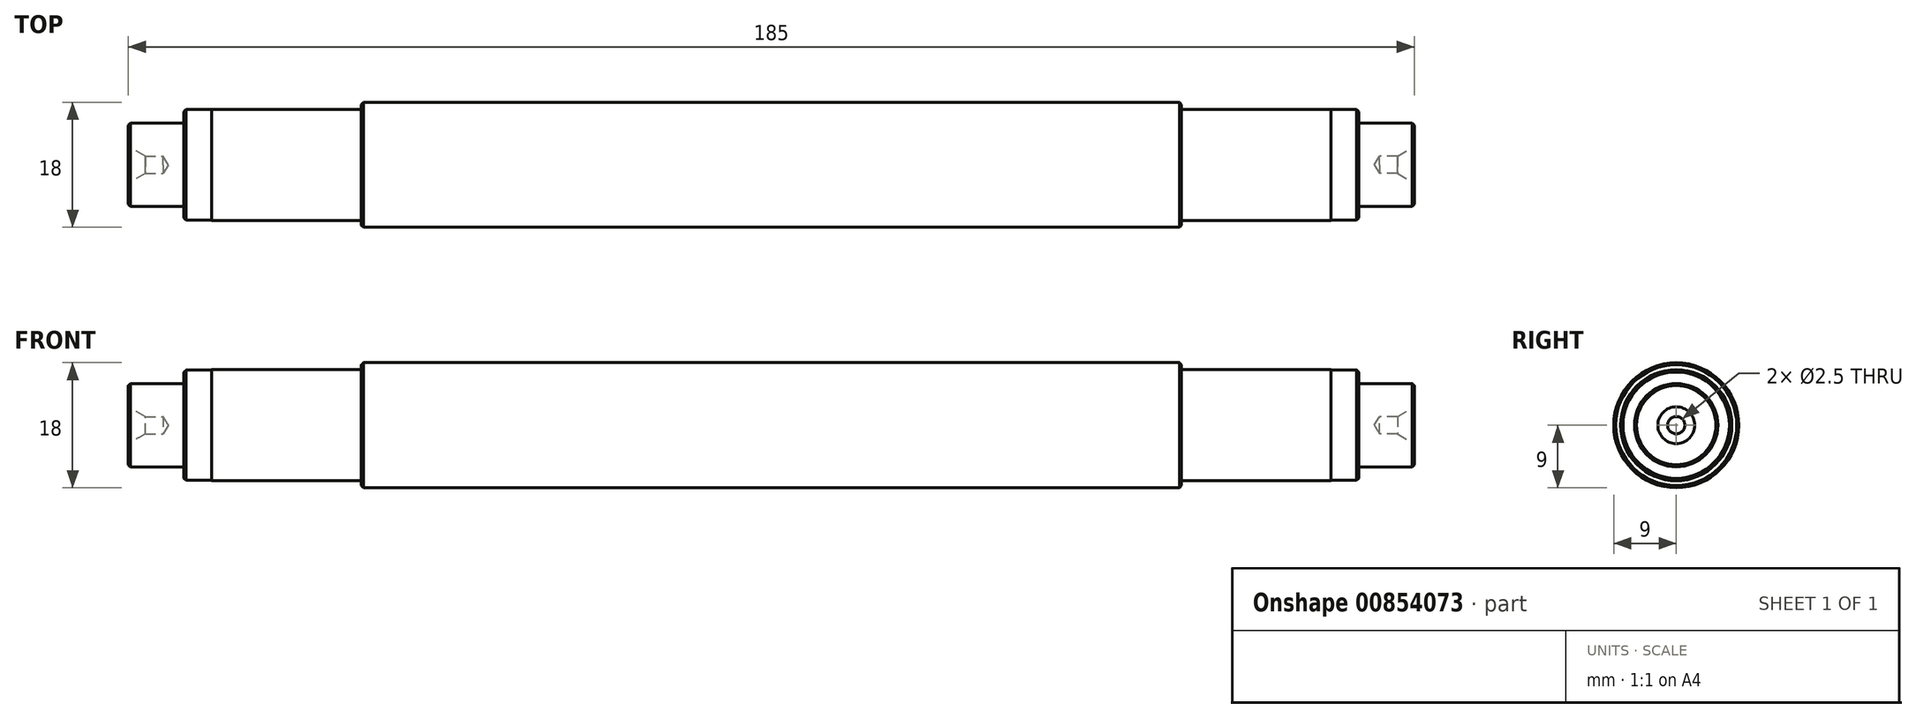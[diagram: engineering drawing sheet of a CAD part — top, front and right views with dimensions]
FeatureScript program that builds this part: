
annotation { "Feature Type Name" : "Feature", "Feature Type Description" : "" }
export const myFeature = defineFeature(function(context is Context, id is Id, definition is map)
    precondition{}
    {
        {
            var Q0;
            Q0=qCreatedBy(makeId("Top.planeOp"),FACE);
            var sketch = newSketch(context, id + "F0", { "sketchPlane" : qUnion([Q0])});
            skLineSegment(sketch, "E0.bottom", {"start": v(0, 0) * mm, "end": v(118, 0) * mm});
            skLineSegment(sketch, "E0.top", {"start": v(0, 9) * mm, "end": v(118, 9) * mm});
            skLineSegment(sketch, "E0.left", {"start": v(0, 0) * mm, "end": v(0, 9) * mm});
            skLineSegment(sketch, "E0.right", {"start": v(118, 0) * mm, "end": v(118, 9) * mm});
            skLineSegment(sketch, "E1.bottom", {"start": v(0, 0) * mm, "end": v(-21.5, 0) * mm});
            skLineSegment(sketch, "E1.top", {"start": v(0, 8) * mm, "end": v(-21.5, 8) * mm});
            skLineSegment(sketch, "E1.left", {"start": v(0, 0) * mm, "end": v(0, 8) * mm});
            skLineSegment(sketch, "E1.right", {"start": v(-21.5, 0) * mm, "end": v(-21.5, 8) * mm});
            skLineSegment(sketch, "E2.bottom", {"start": v(118, 0) * mm, "end": v(139.5, 0) * mm});
            skLineSegment(sketch, "E2.top", {"start": v(118, 8) * mm, "end": v(139.5, 8) * mm});
            skLineSegment(sketch, "E2.left", {"start": v(118, 0) * mm, "end": v(118, 8) * mm});
            skLineSegment(sketch, "E2.right", {"start": v(139.5, 0) * mm, "end": v(139.5, 8) * mm});
            skLineSegment(sketch, "E3.bottom", {"start": v(-21.5, 0) * mm, "end": v(-25.5, 0) * mm});
            skLineSegment(sketch, "E3.top", {"start": v(-21.5, 7.95) * mm, "end": v(-25.5, 7.95) * mm});
            skLineSegment(sketch, "E3.left", {"start": v(-21.5, 0) * mm, "end": v(-21.5, 7.95) * mm});
            skLineSegment(sketch, "E3.right", {"start": v(-25.5, 0) * mm, "end": v(-25.5, 7.95) * mm});
            skLineSegment(sketch, "E4.bottom", {"start": v(139.5, 0) * mm, "end": v(143.5, 0) * mm});
            skLineSegment(sketch, "E4.top", {"start": v(139.5, 7.95) * mm, "end": v(143.5, 7.95) * mm});
            skLineSegment(sketch, "E4.left", {"start": v(139.5, 0) * mm, "end": v(139.5, 7.95) * mm});
            skLineSegment(sketch, "E4.right", {"start": v(143.5, 0) * mm, "end": v(143.5, 7.95) * mm});
            skLineSegment(sketch, "E5.bottom", {"start": v(-25.5, 0) * mm, "end": v(-33.5, 0) * mm});
            skLineSegment(sketch, "E5.top", {"start": v(-25.5, 6) * mm, "end": v(-33.5, 6) * mm});
            skLineSegment(sketch, "E5.left", {"start": v(-25.5, 0) * mm, "end": v(-25.5, 6) * mm});
            skLineSegment(sketch, "E5.right", {"start": v(-33.5, 0) * mm, "end": v(-33.5, 6) * mm});
            skLineSegment(sketch, "E6.bottom", {"start": v(143.5, 0) * mm, "end": v(151.5, 0) * mm});
            skLineSegment(sketch, "E6.top", {"start": v(143.5, 6) * mm, "end": v(151.5, 6) * mm});
            skLineSegment(sketch, "E6.left", {"start": v(143.5, 0) * mm, "end": v(143.5, 6) * mm});
            skLineSegment(sketch, "E6.right", {"start": v(151.5, 0) * mm, "end": v(151.5, 6) * mm});
            skPoint(sketch, "E7", {"position": v(151.5, 0) * mm});
            skPoint(sketch, "E8", {"position": v(-33.5, 0) * mm});
            skSolve(sketch);
        }
        {
            var Q0;
            Q0=makeQuery(id+"F0.imprint","IMPRINT",FACE,{"disambiguationData":[TD([[makeQuery(id+"F0.imprint","IMPRINT",EDGE,{"derivedFrom":sQuery(id+"F0.wireOp",EDGE,"E6.bottom")}),1.0]])]});
            var Q1;
            Q1=makeQuery(id+"F0.imprint","IMPRINT",FACE,{"disambiguationData":[TD([[makeQuery(id+"F0.imprint","IMPRINT",EDGE,{"derivedFrom":sQuery(id+"F0.wireOp",EDGE,"E4.bottom")}),1.0]])]});
            var Q2;
            Q2=makeQuery(id+"F0.imprint","IMPRINT",FACE,{"disambiguationData":[TD([[makeQuery(id+"F0.imprint","IMPRINT",EDGE,{"derivedFrom":sQuery(id+"F0.wireOp",EDGE,"E2.bottom")}),1.0]])]});
            var Q3;
            Q3=makeQuery(id+"F0.imprint","IMPRINT",FACE,{"disambiguationData":[TD([[makeQuery(id+"F0.imprint","IMPRINT",EDGE,{"derivedFrom":sQuery(id+"F0.wireOp",EDGE,"E0.bottom")}),1.0]])]});
            var Q4;
            Q4=makeQuery(id+"F0.imprint","IMPRINT",FACE,{"disambiguationData":[TD([[makeQuery(id+"F0.imprint","IMPRINT",EDGE,{"derivedFrom":sQuery(id+"F0.wireOp",EDGE,"E1.bottom")}),-1.0]])]});
            var Q5;
            Q5=makeQuery(id+"F0.imprint","IMPRINT",FACE,{"disambiguationData":[TD([[makeQuery(id+"F0.imprint","IMPRINT",EDGE,{"derivedFrom":sQuery(id+"F0.wireOp",EDGE,"E3.bottom")}),-1.0]])]});
            var Q6;
            Q6=makeQuery(id+"F0.imprint","IMPRINT",FACE,{"disambiguationData":[TD([[makeQuery(id+"F0.imprint","IMPRINT",EDGE,{"derivedFrom":sQuery(id+"F0.wireOp",EDGE,"E5.bottom")}),-1.0]])]});
            var Q7;
            Q7=sQuery(id+"F0.wireOp",EDGE,"E0.bottom");
            revolve(context, id + "F1", {"surfaceOperationType" : NewSurfaceOperationType.NEW, "entities" : qUnion([Q0, Q1, Q2, Q3, Q4, Q5, Q6]), "axis" : qUnion([Q7]), "revolveType" : RevolveType.ONE_DIRECTION, "angle" : 360 * degree});
        }
        {
            var Q0;
            Q0=makeQuery(id+"F1.opRevolve","SWEPT_EDGE",EDGE,{"disambiguationData":[OSD([sQuery(id+"F0.wireOp",EDGE,"E6.top"),sQuery(id+"F0.wireOp",EDGE,"E6.right")])]});
            var Q1;
            Q1=makeQuery(id+"F1.opRevolve","SWEPT_EDGE",EDGE,{"disambiguationData":[OSD([sQuery(id+"F0.wireOp",EDGE,"E4.top"),sQuery(id+"F0.wireOp",EDGE,"E4.right")])]});
            var Q2;
            Q2=makeQuery(id+"F1.opRevolve","SWEPT_EDGE",EDGE,{"disambiguationData":[OSD([sQuery(id+"F0.wireOp",EDGE,"E0.top"),sQuery(id+"F0.wireOp",EDGE,"E0.right")])]});
            var Q3;
            Q3=makeQuery(id+"F1.opRevolve","SWEPT_EDGE",EDGE,{"disambiguationData":[OSD([sQuery(id+"F0.wireOp",EDGE,"E0.top"),sQuery(id+"F0.wireOp",EDGE,"E0.left")])]});
            var Q4;
            Q4=makeQuery(id+"F1.opRevolve","SWEPT_EDGE",EDGE,{"disambiguationData":[OSD([sQuery(id+"F0.wireOp",EDGE,"E3.top"),sQuery(id+"F0.wireOp",EDGE,"E3.right")])]});
            var Q5;
            Q5=makeQuery(id+"F1.opRevolve","SWEPT_EDGE",EDGE,{"disambiguationData":[OSD([sQuery(id+"F0.wireOp",EDGE,"E5.top"),sQuery(id+"F0.wireOp",EDGE,"E5.right")])]});
            chamfer(context, id + "F2", {"entities" : qUnion([Q0, Q1, Q2, Q3, Q4, Q5]), "width" : 0.3 * mm, "tangentPropagation" : true});
        }
        {
            var Q0;
            Q0=makeQuery(id+"F1.opRevolve","SWEPT_FACE",FACE,{"disambiguationData":[OSD([sQuery(id+"F0.wireOp",EDGE,"E5.right")])]});
            var sketch = newSketch(context, id + "F3", { "sketchPlane" : qUnion([Q0])});
            skPoint(sketch, "E9", {"position": v(0, 0) * mm});
            skSolve(sketch);
        }
        {
            var Q0;
            Q0=makeQuery(id+"F1.opRevolve","SWEPT_FACE",FACE,{"disambiguationData":[OSD([sQuery(id+"F0.wireOp",EDGE,"E6.right")])]});
            var sketch = newSketch(context, id + "F4", { "sketchPlane" : qUnion([Q0])});
            skPoint(sketch, "E10", {"position": v(0, 0) * mm});
            skSolve(sketch);
        }
        {
            var Q0;
            Q0=sQuery(id+"F3.wireOp",VERTEX,"E9");
            var Q1;
            Q1=sQuery(id+"F4.wireOp",VERTEX,"E10");
            var Q2;
            Q2=makeQuery(id+"F1.opRevolve","SWEPT_BODY",BODY,{"disambiguationData":[OSD([sQuery(id+"F0.wireOp",EDGE,"E0.bottom"),sQuery(id+"F0.wireOp",EDGE,"E0.top"),sQuery(id+"F0.wireOp",EDGE,"E0.left"),sQuery(id+"F0.wireOp",EDGE,"E0.right"),sQuery(id+"F0.wireOp",EDGE,"E1.bottom"),sQuery(id+"F0.wireOp",EDGE,"E1.top"),sQuery(id+"F0.wireOp",EDGE,"E1.right"),sQuery(id+"F0.wireOp",EDGE,"E2.bottom"),sQuery(id+"F0.wireOp",EDGE,"E2.top"),sQuery(id+"F0.wireOp",EDGE,"E2.right"),sQuery(id+"F0.wireOp",EDGE,"E3.bottom"),sQuery(id+"F0.wireOp",EDGE,"E3.top"),sQuery(id+"F0.wireOp",EDGE,"E3.right"),sQuery(id+"F0.wireOp",EDGE,"E4.bottom"),sQuery(id+"F0.wireOp",EDGE,"E4.top"),sQuery(id+"F0.wireOp",EDGE,"E4.right"),sQuery(id+"F0.wireOp",EDGE,"E5.bottom"),sQuery(id+"F0.wireOp",EDGE,"E5.top"),sQuery(id+"F0.wireOp",EDGE,"E5.right"),sQuery(id+"F0.wireOp",EDGE,"E6.bottom"),sQuery(id+"F0.wireOp",EDGE,"E6.top"),sQuery(id+"F0.wireOp",EDGE,"E6.right")])]});
            hole(context, id + "F5", {"style" : HoleStyle.C_SINK, "endStyle" : HoleEndStyle.BLIND, "standardTappedOrClearance" : lookupTablePath({ "standard" : "ISO", "size" : "2.5", "type" : "Drilled" }), "standardBlindInLast" : lookupTablePath({ "standard" : "ISO", "size" : "2.5", "type" : "Drilled" }), "holeDiameter" : 2.5 * mm, "cSinkDiameter" : 5.3 * mm, "cSinkAngle" : 60 * degree, "majorDiameter" : 5 * mm, "holeDepth" : 5 * mm, "isTappedThrough" : true, "tappedDepth" : 12 * mm, "tapClearance" : 3, "locations" : qUnion([Q0, Q1]), "scope" : qUnion([Q2]), "startStyle" : HoleStartStyle.SKETCH});
        }
    });
